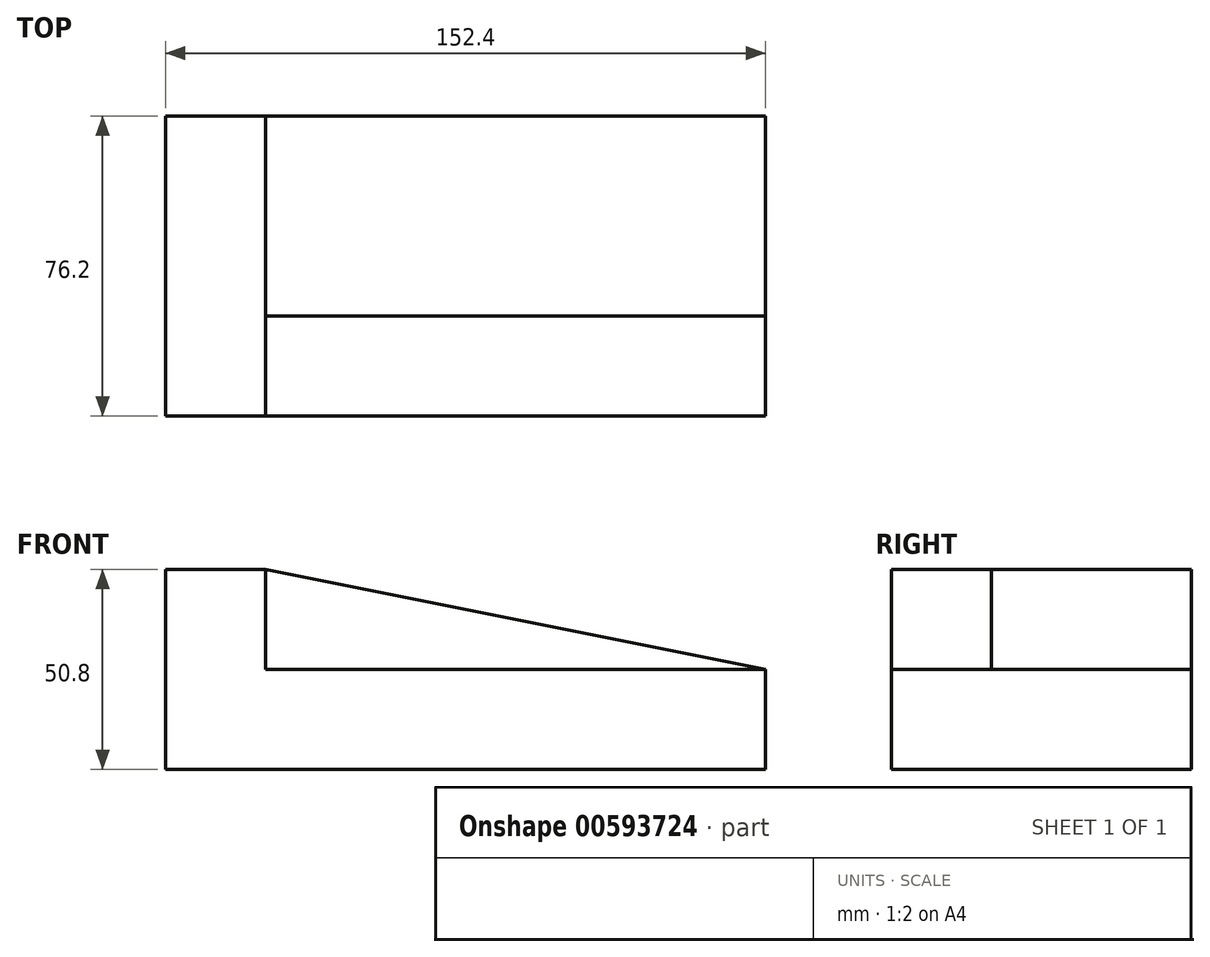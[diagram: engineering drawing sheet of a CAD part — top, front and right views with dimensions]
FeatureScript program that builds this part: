
annotation { "Feature Type Name" : "Feature", "Feature Type Description" : "" }
export const myFeature = defineFeature(function(context is Context, id is Id, definition is map)
    precondition{}
    {
        {
            var Q0;
            Q0=qCreatedBy(makeId("Front.planeOp"),FACE);
            var sketch = newSketch(context, id + "F0", { "sketchPlane" : qUnion([Q0])});
            skLineSegment(sketch, "E0", {"start": v(0, 0) * mm, "end": v(0, 50.8) * mm});
            skLineSegment(sketch, "E1", {"start": v(0, 50.8) * mm, "end": v(152.4, 50.8) * mm});
            skLineSegment(sketch, "E2", {"start": v(152.4, 50.8) * mm, "end": v(152.4, 0) * mm});
            skLineSegment(sketch, "E3", {"start": v(152.4, 0) * mm, "end": v(0, 0) * mm});
            skSolve(sketch);
        }
        {
            var Q0;
            Q0 = qSketchRegion(id + "F0", true);
            extrude(context, id + "F1", {"entities" : qUnion([Q0]), "depth" : 76.2 * mm, "offsetDistance" : 25.4 * mm});
        }
        {
            var Q0;
            Q0=makeQuery(id+"F1.opExtrude","CAP_FACE",FACE,{"disambiguationData":[OSD([sQuery(id+"F0.wireOp",EDGE,"E0"),sQuery(id+"F0.wireOp",EDGE,"E1"),sQuery(id+"F0.wireOp",EDGE,"E2"),sQuery(id+"F0.wireOp",EDGE,"E3")])],"isStart":false});
            var sketch = newSketch(context, id + "F2", { "sketchPlane" : qUnion([Q0])});
            skLineSegment(sketch, "E4", {"start": v(152.4, 25.4) * mm, "end": v(0, 25.4) * mm});
            skLineSegment(sketch, "E5", {"start": v(0, 25.4) * mm, "end": v(0, 50.8) * mm});
            skLineSegment(sketch, "E6", {"start": v(0, 50.8) * mm, "end": v(25.4, 50.8) * mm});
            skLineSegment(sketch, "E7", {"start": v(25.4, 50.8) * mm, "end": v(25.4, 25.4) * mm});
            skLineSegment(sketch, "E8", {"start": v(25.4, 50.8) * mm, "end": v(152.4, 25.4) * mm});
            skSolve(sketch);
        }
        {
            var Q0;
            {var subQ2=sQuery(id+"F2.wireOp",EDGE,"E7");Q0=makeQuery(id+"F2.imprint","IMPRINT",FACE,{"disambiguationData":[TD([[makeQuery(id+"F2.imprint","IMPRINT",EDGE,{"derivedFrom":subQ2}),1.0]])]});}
            var Q1;
            {var subQ0=sQuery(id+"F2.wireOp",EDGE,"E8");Q1=makeQuery(id+"F2.imprint","IMPRINT",FACE,{"disambiguationData":[TD([[makeQuery(id+"F2.imprint","IMPRINT",EDGE,{"derivedFrom":subQ0}),1.0]])]});}
            extrude(context, id + "F3", {"entities" : qUnion([Q0, Q1]), "operationType" : NewBodyOperationType.REMOVE, "oppositeDirection" : true, "depth" : 25.4 * mm, "offsetDistance" : 25.4 * mm});
        }
        {
            var Q0;
            Q0=makeQuery(id+"F1.opExtrude","CAP_FACE",FACE,{"disambiguationData":[OSD([sQuery(id+"F0.wireOp",EDGE,"E0"),sQuery(id+"F0.wireOp",EDGE,"E1"),sQuery(id+"F0.wireOp",EDGE,"E2"),sQuery(id+"F0.wireOp",EDGE,"E3")])],"isStart":true});
            var sketch = newSketch(context, id + "F4", { "sketchPlane" : qUnion([Q0])});
            skLineSegment(sketch, "E9", {"start": v(0, 50.8) * mm, "end": v(0, 25.4) * mm});
            skLineSegment(sketch, "E10", {"start": v(0, 25.4) * mm, "end": v(-25.4, 25.4) * mm});
            skLineSegment(sketch, "E11", {"start": v(-25.4, 25.4) * mm, "end": v(-25.4, 50.8) * mm});
            skLineSegment(sketch, "E12", {"start": v(-25.4, 50.8) * mm, "end": v(-25.4, 25.4) * mm});
            skLineSegment(sketch, "E13", {"start": v(-152.4, 25.4) * mm, "end": v(-25.4, 25.4) * mm});
            skLineSegment(sketch, "E14", {"start": v(-25.4, 50.8) * mm, "end": v(-152.4, 25.4) * mm});
            skSolve(sketch);
        }
        {
            var Q0;
            Q0=makeQuery(id+"F4.imprint","IMPRINT",FACE,{"disambiguationData":[TD([[makeQuery(id+"F4.imprint","IMPRINT",EDGE,{"derivedFrom":sQuery(id+"F4.wireOp",EDGE,"E12")}),-1.0]])]});
            var Q1;
            {var subQ0=sQuery(id+"F4.wireOp",EDGE,"E14");Q1=makeQuery(id+"F4.imprint","IMPRINT",FACE,{"disambiguationData":[TD([[makeQuery(id+"F4.imprint","IMPRINT",EDGE,{"derivedFrom":subQ0}),-1.0]])]});}
            extrude(context, id + "F5", {"entities" : qUnion([Q0, Q1]), "operationType" : NewBodyOperationType.REMOVE, "oppositeDirection" : true, "depth" : 25.4 * mm, "offsetDistance" : 25.4 * mm});
        }
        {
            var Q0;
            Q0=makeQuery(id+"F5.boolean.opBoolean","COPY",FACE,{"derivedFrom":makeQuery(id+"F5.opExtrude","CAP_FACE",FACE,{"disambiguationData":[OSD([sQuery(id+"F0.wireOp",EDGE,"E1"),sQuery(id+"F0.wireOp",EDGE,"E2"),sQuery(id+"F4.wireOp",EDGE,"E12"),sQuery(id+"F4.wireOp",EDGE,"E13")])],"isStart":false})});
            var sketch = newSketch(context, id + "F6", { "sketchPlane" : qUnion([Q0])});
            skLineSegment(sketch, "E15", {"start": v(-25.4, 50.8) * mm, "end": v(-152.4, 25.4) * mm});
            skSolve(sketch);
        }
        {
            var Q0;
            Q0=makeQuery(id+"F6.imprint","IMPRINT",FACE,{"disambiguationData":[TD([[makeQuery(id+"F6.imprint","IMPRINT",EDGE,{"derivedFrom":sQuery(id+"F6.wireOp",EDGE,"E15")}),-1.0]])]});
            extrude(context, id + "F7", {"entities" : qUnion([Q0]), "operationType" : NewBodyOperationType.REMOVE, "oppositeDirection" : true, "depth" : 25.4 * mm, "offsetDistance" : 25.4 * mm});
        }
    });
